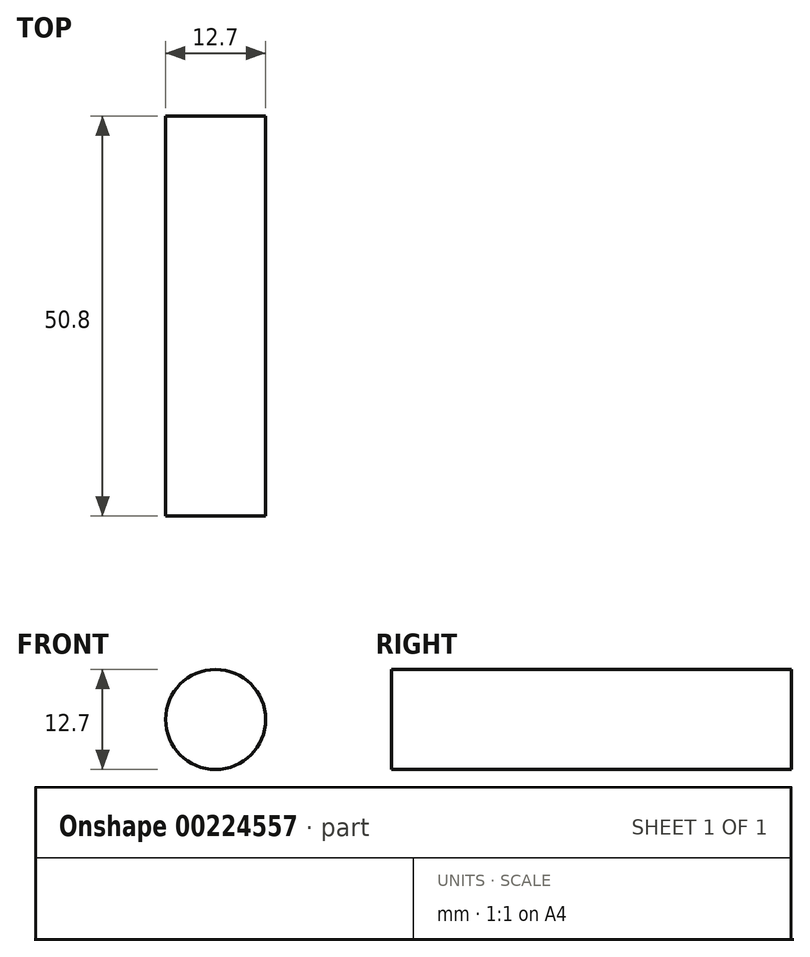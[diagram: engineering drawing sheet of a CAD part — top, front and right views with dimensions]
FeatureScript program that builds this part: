
annotation { "Feature Type Name" : "Feature", "Feature Type Description" : "" }
export const myFeature = defineFeature(function(context is Context, id is Id, definition is map)
    precondition{}
    {
        {
            var Q0;
            Q0=qCreatedBy(makeId("Front.planeOp"),FACE);
            var sketch = newSketch(context, id + "F0", { "sketchPlane" : qUnion([Q0])});
            skCircle(sketch, "E0", {"center": v(-58.24, 32.16) * mm, "radius": 6.35 * mm});
            skSolve(sketch);
        }
        {
            var Q0;
            Q0=makeQuery(id+"F0.imprint","IMPRINT",FACE,{"disambiguationData":[TD([[makeQuery(id+"F0.imprint","IMPRINT",EDGE,{"derivedFrom":sQuery(id+"F0.wireOp",EDGE,"E0")}),1.0]])]});
            extrude(context, id + "F1", {"entities" : qUnion([Q0]), "depth" : 50.8 * mm});
        }
    });
